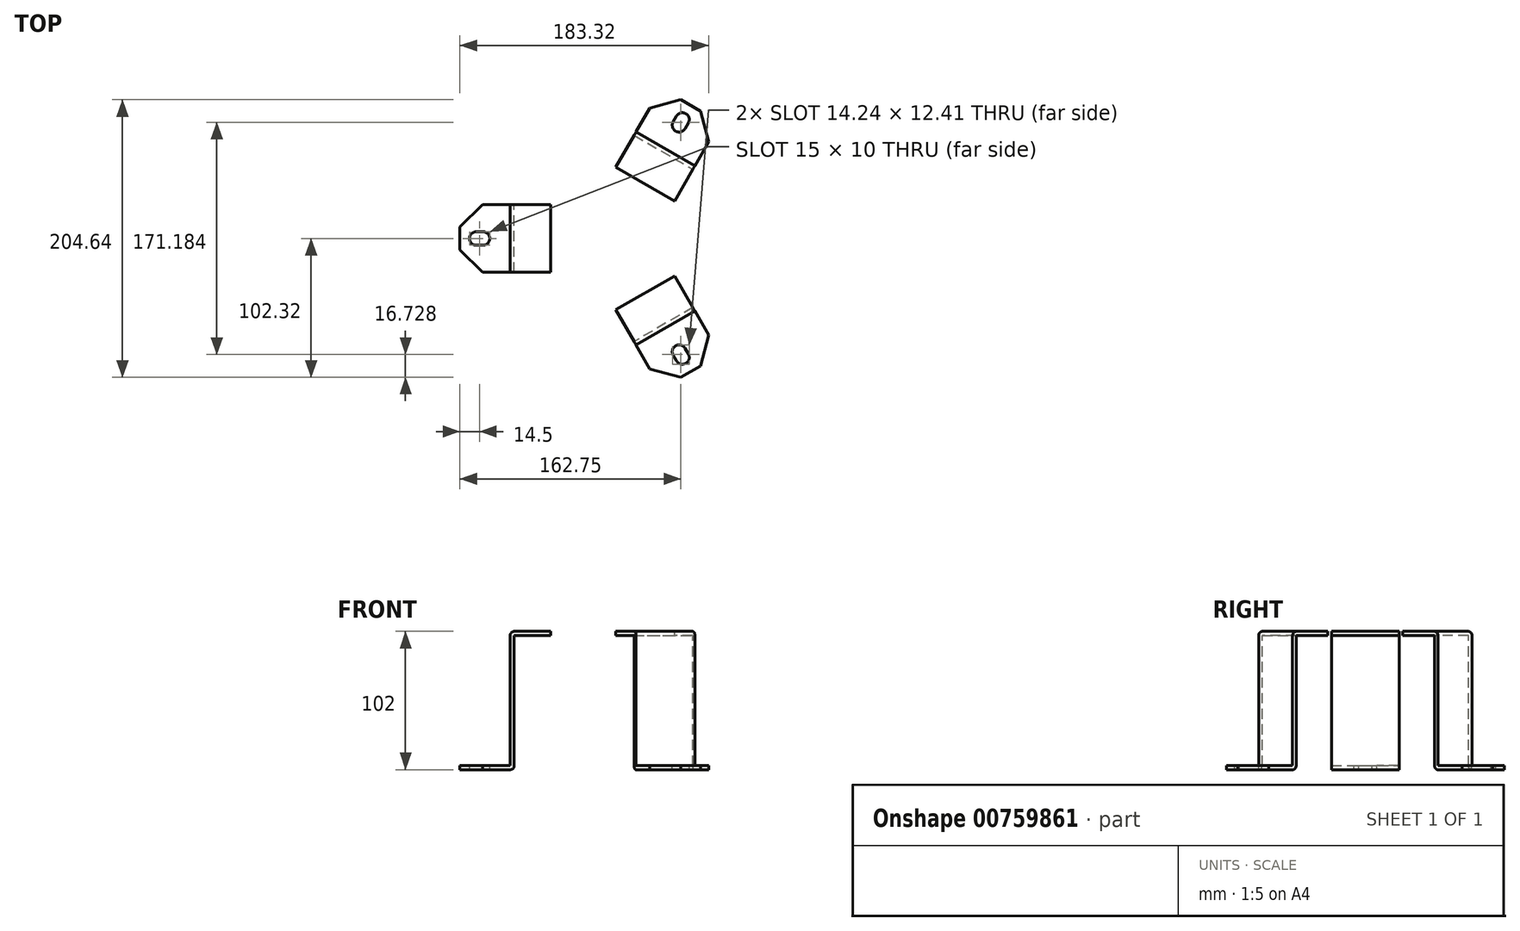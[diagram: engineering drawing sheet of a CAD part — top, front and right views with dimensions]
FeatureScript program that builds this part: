
annotation { "Feature Type Name" : "Feature", "Feature Type Description" : "" }
export const myFeature = defineFeature(function(context is Context, id is Id, definition is map)
    precondition{}
    {
        {
            var Q0;
            Q0=qCreatedBy(makeId("Front.planeOp"),FACE);
            var sketch = newSketch(context, id + "F0", { "sketchPlane" : qUnion([Q0])});
            skLineSegment(sketch, "E0", {"start": v(30, 99) * mm, "end": v(0, 99) * mm});
            skLineSegment(sketch, "E1", {"start": v(0, 99) * mm, "end": v(0, 0) * mm});
            skLineSegment(sketch, "E2", {"start": v(0, 0) * mm, "end": v(-37, 0) * mm});
            skLineSegment(sketch, "E3", {"start": v(-37, 0) * mm, "end": v(-37, -3) * mm});
            skLineSegment(sketch, "E4", {"start": v(-37, -3) * mm, "end": v(3, -3) * mm});
            skLineSegment(sketch, "E5", {"start": v(3, -3) * mm, "end": v(3, 96) * mm});
            skLineSegment(sketch, "E6", {"start": v(3, 96) * mm, "end": v(30, 96) * mm});
            skLineSegment(sketch, "E7", {"start": v(30, 96) * mm, "end": v(30, 99) * mm});
            skSolve(sketch);
        }
        {
            var Q0;
            Q0=makeQuery(id+"F0.imprint","IMPRINT",FACE,{"disambiguationData":[TD([[makeQuery(id+"F0.imprint","IMPRINT",EDGE,{"derivedFrom":sQuery(id+"F0.wireOp",EDGE,"E0")}),1.0]])]});
            extrude(context, id + "F1", {"entities" : qUnion([Q0]), "endBound" : BoundingType.SYMMETRIC, "depth" : 50 * mm, "offsetDistance" : 25 * mm});
        }
        {
            var Q0;
            Q0=makeQuery(id+"F1.opExtrude","SWEPT_FACE",FACE,{"disambiguationData":[OSD([sQuery(id+"F0.wireOp",EDGE,"E2")])]});
            var sketch = newSketch(context, id + "F2", { "sketchPlane" : qUnion([Q0])});
            skLineSegment(sketch, "E8", {"start": v(-20.33, 25) * mm, "end": v(-37, 8.33) * mm});
            skLineSegment(sketch, "E9", {"start": v(-37, 8.33) * mm, "end": v(-37, 25) * mm});
            skLineSegment(sketch, "E10", {"start": v(-37, 25) * mm, "end": v(-20.33, 25) * mm});
            skLineSegment(sketch, "E11.MirrorCS", {"start": v(-20.33, -25) * mm, "end": v(-37, -8.33) * mm});
            skLineSegment(sketch, "E12.MirrorCS", {"start": v(-37, -25) * mm, "end": v(-20.33, -25) * mm});
            skLineSegment(sketch, "E13.MirrorCS", {"start": v(-37, -8.33) * mm, "end": v(-37, -25) * mm});
            skSolve(sketch);
        }
        {
            var Q0;
            Q0=makeQuery(id+"F2.imprint","IMPRINT",FACE,{"disambiguationData":[TD([[makeQuery(id+"F2.imprint","IMPRINT",EDGE,{"derivedFrom":sQuery(id+"F2.wireOp",EDGE,"E8")}),-1.0]])]});
            var Q1;
            Q1=makeQuery(id+"F2.imprint","IMPRINT",FACE,{"disambiguationData":[TD([[makeQuery(id+"F2.imprint","IMPRINT",EDGE,{"derivedFrom":sQuery(id+"F2.wireOp",EDGE,"E11.MirrorCS")}),1.0]])]});
            extrude(context, id + "F3", {"entities" : qUnion([Q0, Q1]), "operationType" : NewBodyOperationType.REMOVE, "oppositeDirection" : true, "depth" : 25 * mm, "offsetDistance" : 25 * mm});
        }
        {
            var Q0;
            Q0=makeQuery(id+"F1.opExtrude","SWEPT_FACE",FACE,{"disambiguationData":[OSD([sQuery(id+"F0.wireOp",EDGE,"E2")])]});
            var sketch = newSketch(context, id + "F4", { "sketchPlane" : qUnion([Q0])});
            skArc(sketch, "E14", {"start": v(-25, 5) * mm, "mid": v(-30, 0) * mm, "end": v(-25, -5) * mm});
            skArc(sketch, "E15", {"start": v(-20, -5) * mm, "mid": v(-15, 0) * mm, "end": v(-20, 5) * mm});
            skLineSegment(sketch, "E16", {"start": v(-25, 5) * mm, "end": v(-20, 5) * mm});
            skLineSegment(sketch, "E17", {"start": v(-25, -5) * mm, "end": v(-20, -5) * mm});
            skSolve(sketch);
        }
        {
            var Q0;
            Q0=makeQuery(id+"F4.imprint","IMPRINT",FACE,{"disambiguationData":[TD([[makeQuery(id+"F4.imprint","IMPRINT",EDGE,{"derivedFrom":sQuery(id+"F4.wireOp",EDGE,"E14")}),1.0]])]});
            extrude(context, id + "F5", {"entities" : qUnion([Q0]), "operationType" : NewBodyOperationType.REMOVE, "oppositeDirection" : true, "depth" : 25 * mm, "offsetDistance" : 25 * mm});
        }
        {
            var Q0;
            Q0=makeQuery(id+"F1.opExtrude","SWEPT_EDGE",EDGE,{"disambiguationData":[OSD([sQuery(id+"F0.wireOp",EDGE,"E4"),sQuery(id+"F0.wireOp",EDGE,"E5")])]});
            var Q1;
            Q1=makeQuery(id+"F1.opExtrude","SWEPT_EDGE",EDGE,{"disambiguationData":[OSD([sQuery(id+"F0.wireOp",EDGE,"E0"),sQuery(id+"F0.wireOp",EDGE,"E1")])]});
            fillet(context, id + "F6", {"entities" : qUnion([Q0, Q1]), "radius" : 3 * mm, "tangentPropagation" : true, "allowEdgeOverflow" : false});
        }
        {
            var Q0;
            Q0=qCreatedBy(makeId("Front.planeOp"),FACE);
            var sketch = newSketch(context, id + "F7", { "sketchPlane" : qUnion([Q0])});
            skLineSegment(sketch, "E18", {"start": v(76.33, 47.08) * mm, "end": v(76.33, -32.46) * mm, "construction": true});
            skPoint(sketch, "E19.0", {"position": v(-28.67, 0) * mm});
            skSolve(sketch);
        }
        {
            var Q0;
            Q0=makeQuery(id+"F1.opExtrude","SWEPT_BODY",BODY,{"disambiguationData":[OSD([sQuery(id+"F0.wireOp",EDGE,"E0"),sQuery(id+"F0.wireOp",EDGE,"E1"),sQuery(id+"F0.wireOp",EDGE,"E2"),sQuery(id+"F0.wireOp",EDGE,"E3"),sQuery(id+"F0.wireOp",EDGE,"E4"),sQuery(id+"F0.wireOp",EDGE,"E5"),sQuery(id+"F0.wireOp",EDGE,"E6"),sQuery(id+"F0.wireOp",EDGE,"E7")])]});
            var Q1;
            Q1=sQuery(id+"F7.wireOp",EDGE,"E18");
            circularPattern(context, id + "F8", {"entities" : qUnion([Q0]), "axis" : qUnion([Q1]), "angle" : 360 * degree, "instanceCount" : 3, "equalSpace" : true});
        }
        {
            var Q0;
            Q0=makeQuery(id+"F1.opExtrude","SWEPT_FACE",FACE,{"disambiguationData":[OSD([sQuery(id+"F0.wireOp",EDGE,"E0")])]});
            cPlane(context, id + "F9", {"entities" : qUnion([Q0]), "cplaneType" : CPlaneType.OFFSET, "offset" : 0 * mm, "width" : 150 * mm, "height" : 150 * mm});
        }
    });
